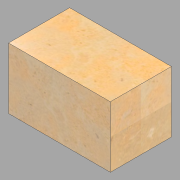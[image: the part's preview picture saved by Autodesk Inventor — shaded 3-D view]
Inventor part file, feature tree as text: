
AUTODESK INVENTOR PART (.ipt)
format: ipt  version: 2022.1 (Build 261234020, 234B)  size: 127,488 bytes
history: native  units: in
note: dims shown in document units (in); Inventor stores cm internally (conversion verified against a paired STEP export)
features: extrude x1, sketch x1
ambient origin geometry x8: Origin, YZ Plane, XZ Plane, XY Plane, X Axis, Y Axis, Z Axis, Center Point
bodies: Solid1 (feature_tree)
feature tree (2):
  extrude  "Extrusion1"  Depth=3.0in
  sketch  "Sketch1"  dims[d0=3.0in d1=3.0in d2=5.0in d3=0.0in]
